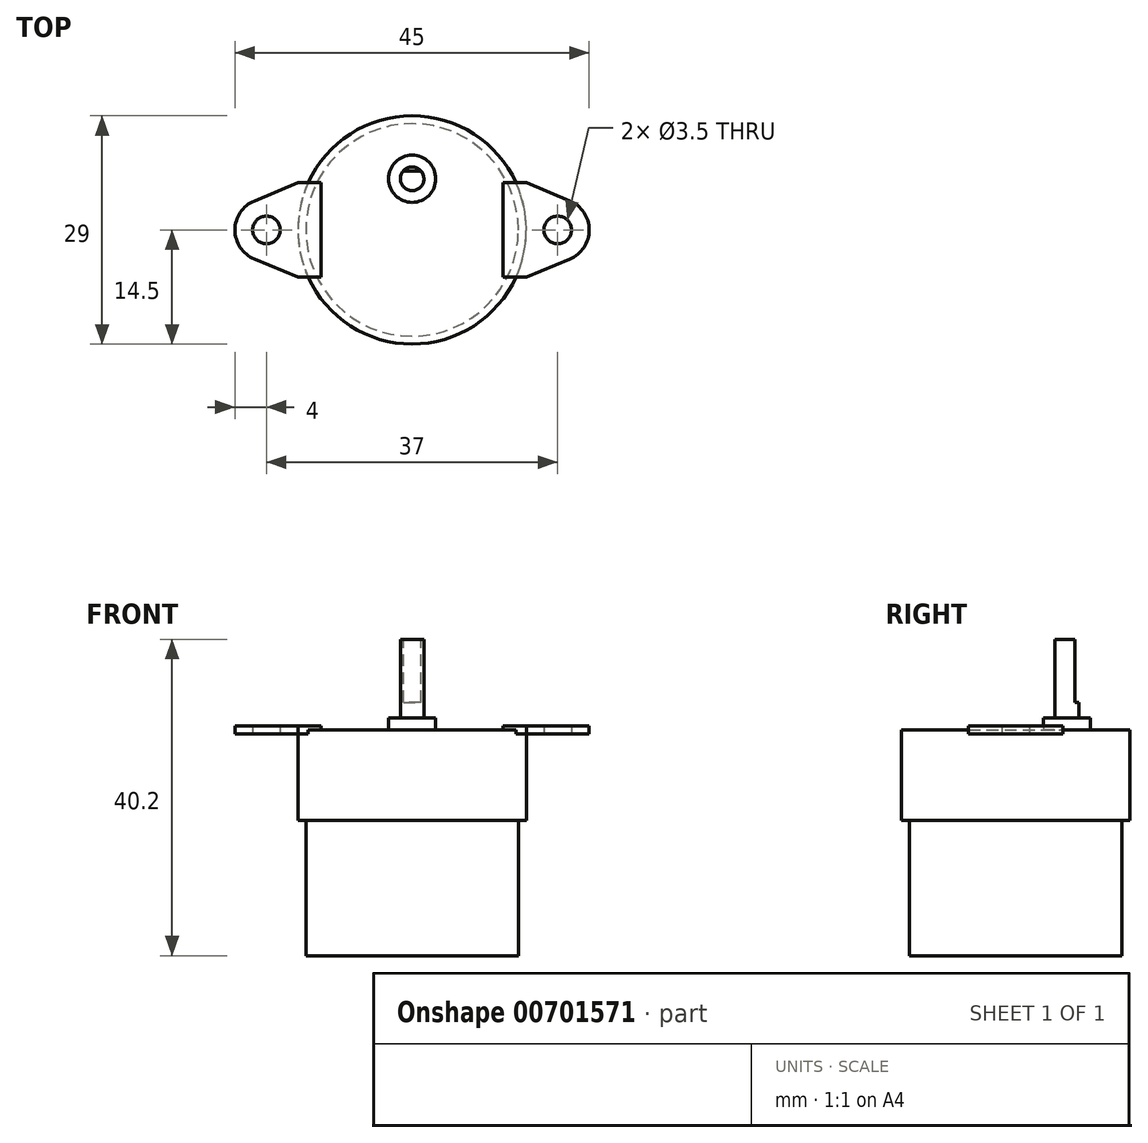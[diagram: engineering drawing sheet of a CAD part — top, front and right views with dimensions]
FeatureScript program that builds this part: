
annotation { "Feature Type Name" : "Feature", "Feature Type Description" : "" }
export const myFeature = defineFeature(function(context is Context, id is Id, definition is map)
    precondition{}
    {
        {
            var Q0;
            Q0=qCreatedBy(makeId("Top.planeOp"),FACE);
            var sketch = newSketch(context, id + "F0", { "sketchPlane" : qUnion([Q0])});
            skCircle(sketch, "E0", {"center": v(0, 0) * mm, "radius": 13.5 * mm});
            skSolve(sketch);
        }
        {
            var Q0;
            Q0 = qSketchRegion(id + "F0", true);
            extrude(context, id + "F1", {"entities" : qUnion([Q0]), "oppositeDirection" : true, "depth" : 17.2 * mm, "offsetDistance" : 25 * mm});
        }
        {
            var Q0;
            Q0=makeQuery(id+"F1.opExtrude","CAP_FACE",FACE,{"disambiguationData":[OSD([sQuery(id+"F0.wireOp",EDGE,"E0")])],"isStart":true});
            var sketch = newSketch(context, id + "F2", { "sketchPlane" : qUnion([Q0])});
            skCircle(sketch, "E1", {"center": v(0, 0) * mm, "radius": 14.5 * mm});
            skSolve(sketch);
        }
        {
            var Q0;
            Q0 = qSketchRegion(id + "F2", true);
            extrude(context, id + "F3", {"entities" : qUnion([Q0]), "operationType" : NewBodyOperationType.ADD, "depth" : 11.5 * mm, "offsetDistance" : 25 * mm});
        }
        {
            var Q0;
            Q0=makeQuery(id+"F3.opExtrude","CAP_FACE",FACE,{"disambiguationData":[OSD([sQuery(id+"F2.wireOp",EDGE,"E1")])],"isStart":false});
            var sketch = newSketch(context, id + "F4", { "sketchPlane" : qUnion([Q0])});
            skLineSegment(sketch, "E2", {"start": v(-14.5, 6) * mm, "end": v(-20.04, 3.7) * mm});
            skLineSegment(sketch, "E3", {"start": v(-20.04, -3.7) * mm, "end": v(-14.5, -6) * mm});
            skLineSegment(sketch, "E4", {"start": v(-14.5, -6) * mm, "end": v(-14.5, 6) * mm});
            skCircle(sketch, "E5", {"center": v(-18.5, 0) * mm, "radius": 1.75 * mm});
            skPoint(sketch, "E6", {"position": v(-14.5, 0) * mm});
            skLineSegment(sketch, "E7", {"start": v(-14.5, 6) * mm, "end": v(-11.54, 6) * mm});
            skLineSegment(sketch, "E8", {"start": v(-11.54, 6) * mm, "end": v(-11.54, -6) * mm});
            skLineSegment(sketch, "E9", {"start": v(-11.54, -6) * mm, "end": v(-14.5, -6) * mm});
            skPoint(sketch, "E10.visualSharp", {"position": v(-28.9, 0) * mm});
            skArc(sketch, "E10.filletArc", {"start": v(-20.04, 3.7) * mm, "mid": v(-22.5, 0) * mm, "end": v(-20.04, -3.7) * mm});
            skLineSegment(sketch, "E11", {"start": v(0, 12.88) * mm, "end": v(0, 18.87) * mm, "construction": true});
            skArc(sketch, "E12.MirrorCS", {"start": v(20.04, 3.7) * mm, "mid": v(22.5, 0) * mm, "end": v(20.04, -3.7) * mm});
            skLineSegment(sketch, "E13.MirrorCS", {"start": v(11.54, -6) * mm, "end": v(14.5, -6) * mm});
            skLineSegment(sketch, "E14.MirrorCS", {"start": v(11.54, 6) * mm, "end": v(11.54, -6) * mm});
            skLineSegment(sketch, "E15.MirrorCS", {"start": v(14.5, 6) * mm, "end": v(20.04, 3.7) * mm});
            skLineSegment(sketch, "E16.MirrorCS", {"start": v(14.5, 6) * mm, "end": v(11.54, 6) * mm});
            skLineSegment(sketch, "E17.MirrorCS", {"start": v(20.04, -3.7) * mm, "end": v(14.5, -6) * mm});
            skLineSegment(sketch, "E18.MirrorCS", {"start": v(14.5, -6) * mm, "end": v(14.5, 6) * mm});
            skPoint(sketch, "E19.MirrorP", {"position": v(14.5, 0) * mm});
            skCircle(sketch, "E20.MirrorC", {"center": v(18.5, 0) * mm, "radius": 1.75 * mm});
            skSolve(sketch);
        }
        {
            var Q0;
            Q0 = qSketchRegion(id + "F4", true);
            extrude(context, id + "F5", {"entities" : qUnion([Q0]), "operationType" : NewBodyOperationType.ADD, "endBound" : BoundingType.SYMMETRIC, "depth" : 1 * mm, "offsetDistance" : 25 * mm});
        }
        {
            var Q0;
            Q0=makeQuery(id+"F3.opExtrude","CAP_FACE",FACE,{"disambiguationData":[OSD([sQuery(id+"F2.wireOp",EDGE,"E1")])],"isStart":false});
            var sketch = newSketch(context, id + "F6", { "sketchPlane" : qUnion([Q0])});
            skCircle(sketch, "E21", {"center": v(0, 6.5) * mm, "radius": 3 * mm});
            skSolve(sketch);
        }
        {
            var Q0;
            Q0 = qSketchRegion(id + "F6", true);
            extrude(context, id + "F7", {"entities" : qUnion([Q0]), "operationType" : NewBodyOperationType.ADD, "depth" : 1.5 * mm, "offsetDistance" : 25 * mm});
        }
        {
            var Q0;
            Q0=makeQuery(id+"F7.opExtrude","CAP_FACE",FACE,{"disambiguationData":[OSD([sQuery(id+"F6.wireOp",EDGE,"E21")])],"isStart":false});
            var sketch = newSketch(context, id + "F8", { "sketchPlane" : qUnion([Q0])});
            skCircle(sketch, "E22", {"center": v(0, 6.5) * mm, "radius": 1.5 * mm});
            skSolve(sketch);
        }
        {
            var Q0;
            Q0 = qSketchRegion(id + "F8", true);
            extrude(context, id + "F9", {"entities" : qUnion([Q0]), "operationType" : NewBodyOperationType.ADD, "depth" : 10 * mm, "offsetDistance" : 25 * mm});
        }
        {
            var Q0;
            Q0=makeQuery(id+"F9.opExtrude","CAP_FACE",FACE,{"disambiguationData":[OSD([sQuery(id+"F8.wireOp",EDGE,"E22")])],"isStart":false});
            var sketch = newSketch(context, id + "F10", { "sketchPlane" : qUnion([Q0])});
            skLineSegment(sketch, "E23", {"start": v(-1.12, 7.5) * mm, "end": v(1.12, 7.5) * mm});
            skLineSegment(sketch, "E24", {"start": v(1.12, 7.5) * mm, "end": v(1.12, 9.24) * mm});
            skLineSegment(sketch, "E25", {"start": v(1.12, 9.24) * mm, "end": v(-1.12, 9.24) * mm});
            skLineSegment(sketch, "E26", {"start": v(-1.12, 9.24) * mm, "end": v(-1.12, 7.5) * mm});
            skPoint(sketch, "E27", {"position": v(0, 5) * mm});
            skSolve(sketch);
        }
        {
            var Q0;
            Q0 = qSketchRegion(id + "F10", true);
            extrude(context, id + "F11", {"entities" : qUnion([Q0]), "operationType" : NewBodyOperationType.REMOVE, "oppositeDirection" : true, "depth" : 8 * mm, "offsetDistance" : 25 * mm});
        }
    });
